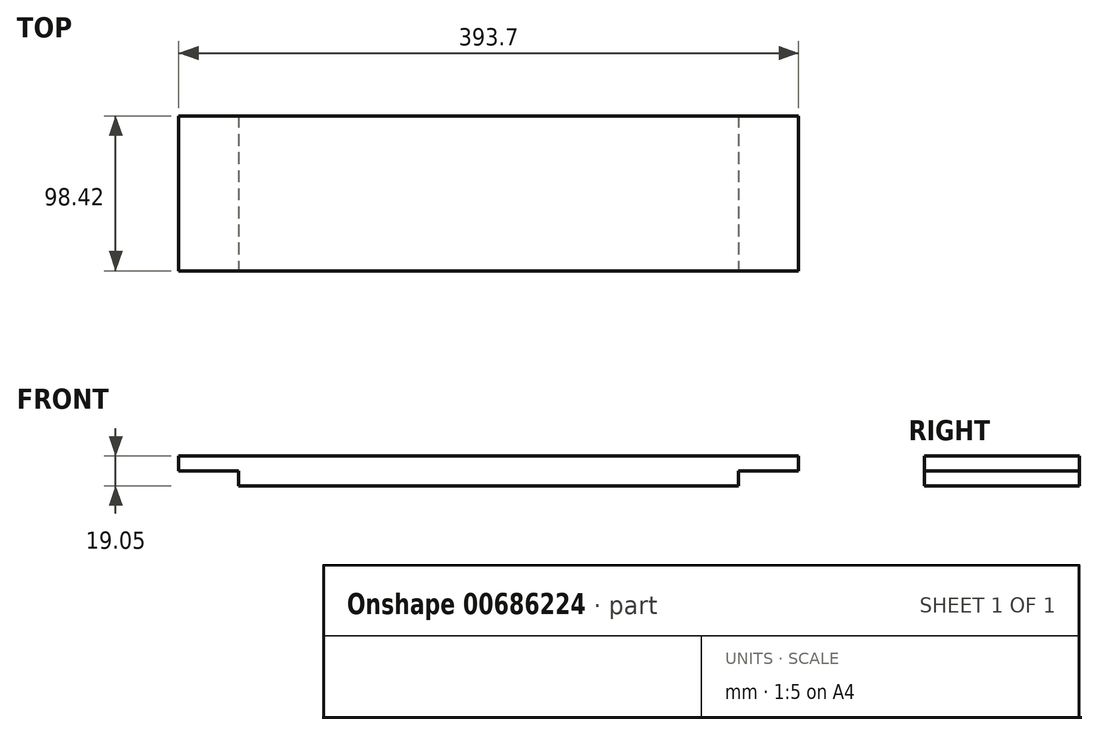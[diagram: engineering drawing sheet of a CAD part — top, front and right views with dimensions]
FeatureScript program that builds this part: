
annotation { "Feature Type Name" : "Feature", "Feature Type Description" : "" }
export const myFeature = defineFeature(function(context is Context, id is Id, definition is map)
    precondition{}
    {
        {
            var Q0;
            Q0=qCreatedBy(makeId("Top.planeOp"),FACE);
            var sketch = newSketch(context, id + "F0", { "sketchPlane" : qUnion([Q0])});
            skLineSegment(sketch, "E0.bottom", {"start": v(-196.85, 49.21) * mm, "end": v(196.85, 49.21) * mm});
            skLineSegment(sketch, "E0.top", {"start": v(-196.85, -49.21) * mm, "end": v(196.85, -49.21) * mm});
            skLineSegment(sketch, "E0.left", {"start": v(-196.85, 49.21) * mm, "end": v(-196.85, -49.21) * mm});
            skLineSegment(sketch, "E0.right", {"start": v(196.85, 49.21) * mm, "end": v(196.85, -49.21) * mm});
            skPoint(sketch, "E0.middle", {"position": v(0, 0) * mm});
            skSolve(sketch);
        }
        {
            var Q0;
            Q0 = qSketchRegion(id + "F0", true);
            extrude(context, id + "F1", {"entities" : qUnion([Q0]), "depth" : 19.05 * mm, "offsetDistance" : 25.4 * mm});
        }
        {
            var Q0;
            Q0=qCreatedBy(makeId("Front.planeOp"),FACE);
            var sketch = newSketch(context, id + "F2", { "sketchPlane" : qUnion([Q0])});
            skLineSegment(sketch, "E1", {"start": v(0, 19.05) * mm, "end": v(0, 0) * mm, "construction": true});
            skPoint(sketch, "E2", {"position": v(0, 9.53) * mm});
            skSolve(sketch);
        }
        {
            var Q0;
            Q0=qCreatedBy(makeId("Top.planeOp"),FACE);
            var Q1;
            Q1=sQuery(id+"F2.wireOp",VERTEX,"E2");
            cPlane(context, id + "F3", {"entities" : qUnion([Q0, Q1]), "cplaneType" : CPlaneType.PLANE_POINT, "offset" : 0 * mm, "width" : 152.4 * mm, "height" : 152.4 * mm});
        }
        {
            var Q0;
            Q0=qCreatedBy(id+"F3.planeOp",FACE);
            var sketch = newSketch(context, id + "F4", { "sketchPlane" : qUnion([Q0])});
            skLineSegment(sketch, "E3.bottom", {"start": v(-196.85, -49.21) * mm, "end": v(-158.75, -49.21) * mm});
            skLineSegment(sketch, "E3.top", {"start": v(-196.85, 49.21) * mm, "end": v(-158.75, 49.21) * mm});
            skLineSegment(sketch, "E3.left", {"start": v(-196.85, 49.21) * mm, "end": v(-196.85, -49.21) * mm});
            skLineSegment(sketch, "E3.right", {"start": v(-158.75, 49.21) * mm, "end": v(-158.75, -49.21) * mm});
            skLineSegment(sketch, "E4.bottom", {"start": v(196.85, -49.21) * mm, "end": v(158.75, -49.21) * mm});
            skLineSegment(sketch, "E4.top", {"start": v(196.85, 49.21) * mm, "end": v(158.75, 49.21) * mm});
            skLineSegment(sketch, "E4.left", {"start": v(196.85, 49.21) * mm, "end": v(196.85, -49.21) * mm});
            skLineSegment(sketch, "E4.right", {"start": v(158.75, 49.21) * mm, "end": v(158.75, -49.21) * mm});
            skSolve(sketch);
        }
        {
            var Q0;
            Q0 = qSketchRegion(id + "F4", true);
            extrude(context, id + "F5", {"entities" : qUnion([Q0]), "operationType" : NewBodyOperationType.REMOVE, "endBound" : BoundingType.THROUGH_ALL, "oppositeDirection" : true, "depth" : 6.35 * mm, "offsetDistance" : 25.4 * mm});
        }
    });
